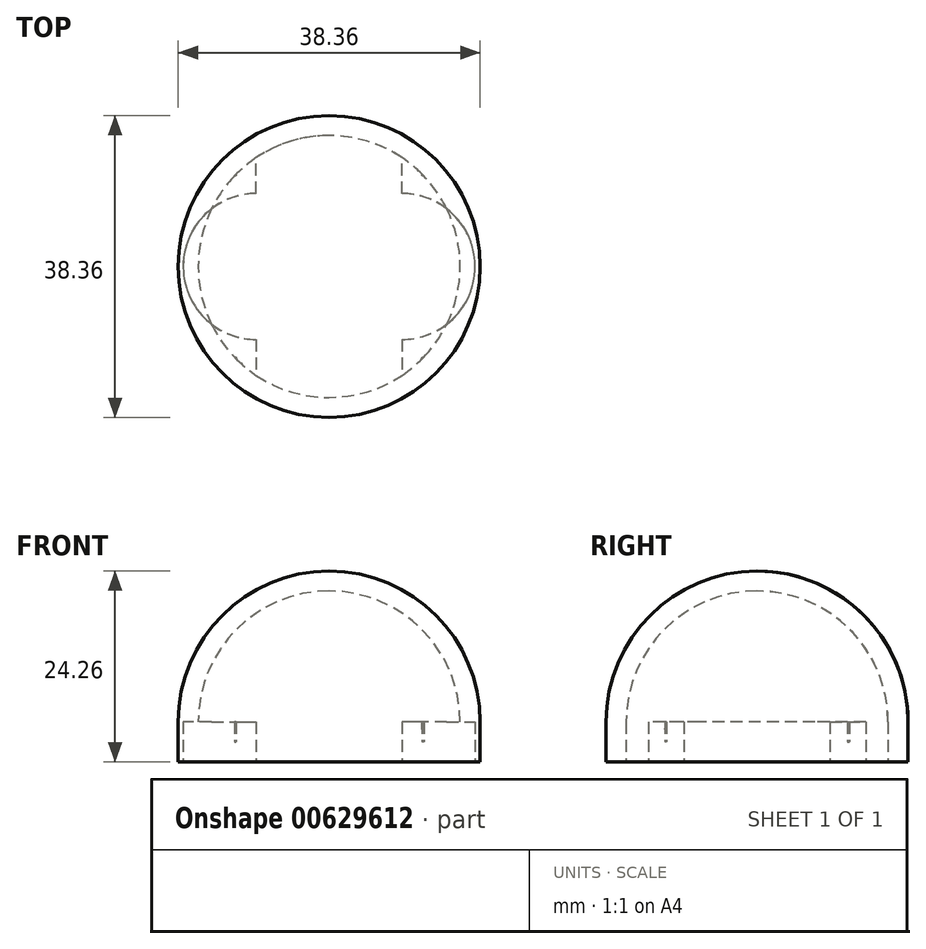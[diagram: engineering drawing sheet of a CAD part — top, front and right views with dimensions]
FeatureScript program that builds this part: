
annotation { "Feature Type Name" : "Feature", "Feature Type Description" : "" }
export const myFeature = defineFeature(function(context is Context, id is Id, definition is map)
    precondition{}
    {
        {
            var Q0;
            Q0=qCreatedBy(makeId("Top.planeOp"),FACE);
            var sketch = newSketch(context, id + "F0", { "sketchPlane" : qUnion([Q0])});
            skLineSegment(sketch, "E0.bottom", {"start": v(-9.27, 9.27) * mm, "end": v(9.27, 9.27) * mm, "construction": true});
            skLineSegment(sketch, "E0.top", {"start": v(-9.27, -9.27) * mm, "end": v(9.27, -9.27) * mm, "construction": true});
            skLineSegment(sketch, "E0.left", {"start": v(-9.27, 9.27) * mm, "end": v(-9.27, -9.27) * mm, "construction": true});
            skLineSegment(sketch, "E0.right", {"start": v(9.27, 9.27) * mm, "end": v(9.27, -9.27) * mm, "construction": true});
            skPoint(sketch, "E0.middle", {"position": v(0, 0) * mm});
            skArc(sketch, "E1", {"start": v(-9.27, 9.27) * mm, "mid": v(-18.54, 0) * mm, "end": v(-9.27, -9.27) * mm});
            skArc(sketch, "E2", {"start": v(9.27, -9.27) * mm, "mid": v(18.54, 0) * mm, "end": v(9.27, 9.27) * mm});
            skCircle(sketch, "E3", {"center": v(0, 0) * mm, "radius": 19.18 * mm});
            skLineSegment(sketch, "E4", {"start": v(-9.27, -9.27) * mm, "end": v(-9.27, -13.81) * mm});
            skLineSegment(sketch, "E5", {"start": v(9.27, -9.27) * mm, "end": v(9.27, -13.81) * mm});
            skArc(sketch, "E6", {"start": v(-9.27, -13.81) * mm, "mid": v(0, -16.64) * mm, "end": v(9.27, -13.81) * mm});
            skLineSegment(sketch, "E7", {"start": v(-9.27, 9.27) * mm, "end": v(-9.27, 13.81) * mm});
            skLineSegment(sketch, "E8", {"start": v(9.27, 9.27) * mm, "end": v(9.27, 13.81) * mm});
            skArc(sketch, "E9", {"start": v(9.27, 13.81) * mm, "mid": v(0, 16.64) * mm, "end": v(-9.27, 13.81) * mm});
            skPoint(sketch, "E10", {"position": v(0, 19.18) * mm});
            skPoint(sketch, "E11", {"position": v(0, 16.64) * mm});
            skSolve(sketch);
        }
        {
            var Q0;
            Q0 = qSketchRegion(id + "F0", true);
            extrude(context, id + "F1", {"entities" : qUnion([Q0]), "depth" : 5.08 * mm, "offsetDistance" : 25.4 * mm});
        }
        {
            var Q0;
            Q0=qCreatedBy(makeId("Right.planeOp"),FACE);
            var sketch = newSketch(context, id + "F2", { "sketchPlane" : qUnion([Q0])});
            skArc(sketch, "E12", {"start": v(0, 24.26) * mm, "mid": v(-13.56, 18.64) * mm, "end": v(-19.18, 5.08) * mm});
            skLineSegment(sketch, "E13", {"start": v(-19.18, 5.08) * mm, "end": v(-19.18, 0) * mm, "construction": true});
            skLineSegment(sketch, "E14", {"start": v(0, 24.26) * mm, "end": v(0, 5.08) * mm});
            skLineSegment(sketch, "E15", {"start": v(-19.18, 5.08) * mm, "end": v(0, 5.08) * mm});
            skSolve(sketch);
        }
        {
            var Q0;
            Q0 = qSketchRegion(id + "F2", true);
            var Q1;
            Q1=sQuery(id+"F2.wireOp",EDGE,"E14");
            revolve(context, id + "F3", {"operationType" : NewBodyOperationType.ADD, "entities" : qUnion([Q0]), "axis" : qUnion([Q1]), "revolveType" : RevolveType.FULL});
        }
        {
            var Q0;
            Q0=makeQuery(id+"F3.opRevolve","SWEPT_FACE",FACE,{"disambiguationData":[OSD([sQuery(id+"F2.wireOp",EDGE,"E15")])]});
            shell(context, id + "F4", {"entities" : qUnion([Q0]), "thickness" : 2.54 * mm});
        }
        {
            var Q0;
            {var subQ0=sQuery(id+"F0.wireOp",EDGE,"E2");Q0=makeQuery(id+"F4.opShell","OFFSET_EDGE",EDGE,{"disambiguationData":[OSD([subQ0]),TDD([makeQuery(id+"F1.opExtrude","CAP_EDGE",EDGE,{"disambiguationData":[OSD([subQ0])],"isStart":false})]),OD(0.0)]});}
            var Q1;
            {var subQ0=sQuery(id+"F0.wireOp",EDGE,"E1");Q1=makeQuery(id+"F4.opShell","OFFSET_EDGE",EDGE,{"disambiguationData":[OSD([subQ0]),TDD([makeQuery(id+"F1.opExtrude","CAP_EDGE",EDGE,{"disambiguationData":[OSD([subQ0])],"isStart":false})]),OD(0.0)]});}
            fillet(context, id + "F5", {"entities" : qUnion([Q0, Q1]), "radius" : 2.54 * mm, "tangentPropagation" : true, "allowEdgeOverflow" : false});
        }
    });
